# Revit family: Haworth_Kennedee_Sectional_OneArm
name_source: partatom
category: Furniture
revit_build: Autodesk Revit 2018 (Build: 20170223_1515(x64)
units: mm (PartAtom-declared; Revit-internal decimal feet)

## family parameters
Always vertical = Yes
Cut with Voids When Loaded = No
OmniClass Number = 23.40.70.14.64.21
OmniClass Title = Systems Furniture
Room Calculation Point = No
Shared = No
Work Plane-Based = No

## types (3) — shared parameters
Actual Depth = 37"
Actual Height = 28 1/4"
Assembly Code = E2020200
Base Finish = Haworth _ Paint _ Metallic Gunmetal
Leg Offset = 10 1/2"
Leg Thickness = 2"
Manufacturer = Haworth
Model = HCPF-KEG
Revision Number = 5
Size = Verify Final Dim. w/ Haworth
URL = http://www.haworth.com
URL - Product = http://www.haworth.com
Warranty = http://www.haworth.com

## per-type parameters (varying)
| type | Actual Width | Description | Leg Offset Left | Middle Seat Control | Middle Seat Offset | One Seat | Seat Width | Three Seats | Two Seats |
| HCPF-KEG2 - Two Seats | 74" | Haworth Kennedee Sectional One Arm - Two Seats | 13 1/2" | Yes | 0" | No | 71" | No | Yes |
| HCPF-KEG1 - One Seat | 38 1/2" | Haworth Kennedee Sectional One Arm - One Seat | 13 1/2" | No | 0" | Yes | 35 1/2" | No | No |
| HCPF-KEG3 - Three Seats | 109 1/2" | Haworth Kennedee Sectional One Arm - Three Seats | 52 1/2" | Yes | 35 1/2" | No | 106 1/2" | Yes | No |

## geometry (parser evidence)
native form markers: Sweep x10
no freeform markers — native parametric forms only
